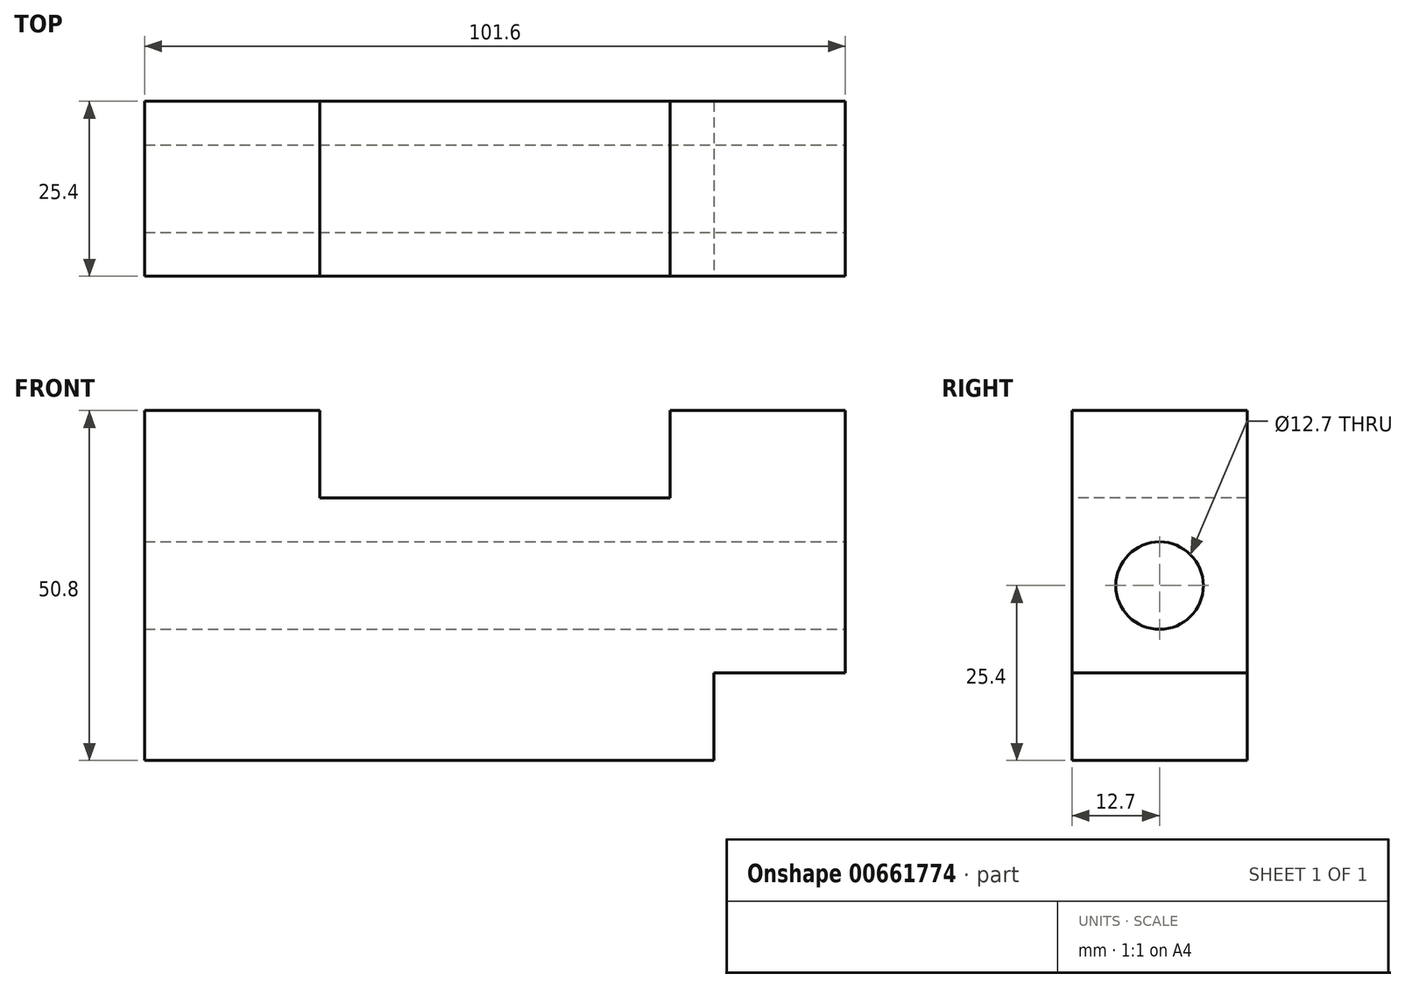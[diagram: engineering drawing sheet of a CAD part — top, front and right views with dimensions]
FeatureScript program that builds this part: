
annotation { "Feature Type Name" : "Feature", "Feature Type Description" : "" }
export const myFeature = defineFeature(function(context is Context, id is Id, definition is map)
    precondition{}
    {
        {
            var Q0;
            Q0=qCreatedBy(makeId("Front.planeOp"),FACE);
            var sketch = newSketch(context, id + "F0", { "sketchPlane" : qUnion([Q0])});
            skLineSegment(sketch, "E0.bottom", {"start": v(50.8, -25.4) * mm, "end": v(-50.8, -25.4) * mm});
            skLineSegment(sketch, "E0.top", {"start": v(50.8, 25.4) * mm, "end": v(-50.8, 25.4) * mm});
            skLineSegment(sketch, "E0.left", {"start": v(50.8, -25.4) * mm, "end": v(50.8, 25.4) * mm});
            skLineSegment(sketch, "E0.right", {"start": v(-50.8, -25.4) * mm, "end": v(-50.8, 25.4) * mm});
            skPoint(sketch, "E0.middle", {"position": v(0, 0) * mm});
            skSolve(sketch);
        }
        {
            var Q0;
            Q0 = qSketchRegion(id + "F0", true);
            extrude(context, id + "F1", {"entities" : qUnion([Q0]), "depth" : 25.4 * mm, "offsetDistance" : 25.4 * mm});
        }
        {
            var Q0;
            Q0=makeQuery(id+"F1.opExtrude","CAP_FACE",FACE,{"disambiguationData":[OSD([sQuery(id+"F0.wireOp",EDGE,"E0.bottom"),sQuery(id+"F0.wireOp",EDGE,"E0.top"),sQuery(id+"F0.wireOp",EDGE,"E0.left"),sQuery(id+"F0.wireOp",EDGE,"E0.right")])],"isStart":false});
            var sketch = newSketch(context, id + "F2", { "sketchPlane" : qUnion([Q0])});
            skLineSegment(sketch, "E1.bottom", {"start": v(-25.4, 25.4) * mm, "end": v(25.4, 25.4) * mm});
            skLineSegment(sketch, "E1.top", {"start": v(-25.4, 12.7) * mm, "end": v(25.4, 12.7) * mm});
            skLineSegment(sketch, "E1.left", {"start": v(-25.4, 25.4) * mm, "end": v(-25.4, 12.7) * mm});
            skLineSegment(sketch, "E1.right", {"start": v(25.4, 25.4) * mm, "end": v(25.4, 12.7) * mm});
            skSolve(sketch);
        }
        {
            var Q0;
            Q0 = qSketchRegion(id + "F2", true);
            extrude(context, id + "F3", {"entities" : qUnion([Q0]), "operationType" : NewBodyOperationType.REMOVE, "endBound" : BoundingType.THROUGH_ALL, "oppositeDirection" : true, "depth" : 25.4 * mm, "offsetDistance" : 25.4 * mm});
        }
        {
            var Q0;
            Q0=makeQuery(id+"F1.opExtrude","CAP_FACE",FACE,{"disambiguationData":[OSD([sQuery(id+"F0.wireOp",EDGE,"E0.bottom"),sQuery(id+"F0.wireOp",EDGE,"E0.top"),sQuery(id+"F0.wireOp",EDGE,"E0.left"),sQuery(id+"F0.wireOp",EDGE,"E0.right")])],"isStart":false});
            var sketch = newSketch(context, id + "F4", { "sketchPlane" : qUnion([Q0])});
            skLineSegment(sketch, "E2.bottom", {"start": v(50.8, -25.4) * mm, "end": v(31.75, -25.4) * mm});
            skLineSegment(sketch, "E2.top", {"start": v(50.8, -12.7) * mm, "end": v(31.75, -12.7) * mm});
            skLineSegment(sketch, "E2.left", {"start": v(50.8, -25.4) * mm, "end": v(50.8, -12.7) * mm});
            skLineSegment(sketch, "E2.right", {"start": v(31.75, -25.4) * mm, "end": v(31.75, -12.7) * mm});
            skSolve(sketch);
        }
        {
            var Q0;
            Q0 = qSketchRegion(id + "F4", true);
            extrude(context, id + "F5", {"entities" : qUnion([Q0]), "operationType" : NewBodyOperationType.REMOVE, "endBound" : BoundingType.THROUGH_ALL, "oppositeDirection" : true, "depth" : 25.4 * mm, "offsetDistance" : 25.4 * mm});
        }
        {
            var Q0;
            Q0=makeQuery(id+"F1.opExtrude","SWEPT_FACE",FACE,{"disambiguationData":[OSD([sQuery(id+"F0.wireOp",EDGE,"E0.left")])]});
            var sketch = newSketch(context, id + "F6", { "sketchPlane" : qUnion([Q0])});
            skCircle(sketch, "E3", {"center": v(-12.7, 0) * mm, "radius": 6.35 * mm});
            skSolve(sketch);
        }
        {
            var Q0;
            Q0 = qSketchRegion(id + "F6", true);
            extrude(context, id + "F7", {"entities" : qUnion([Q0]), "operationType" : NewBodyOperationType.REMOVE, "endBound" : BoundingType.THROUGH_ALL, "oppositeDirection" : true, "depth" : 25.4 * mm, "offsetDistance" : 25.4 * mm});
        }
    });
